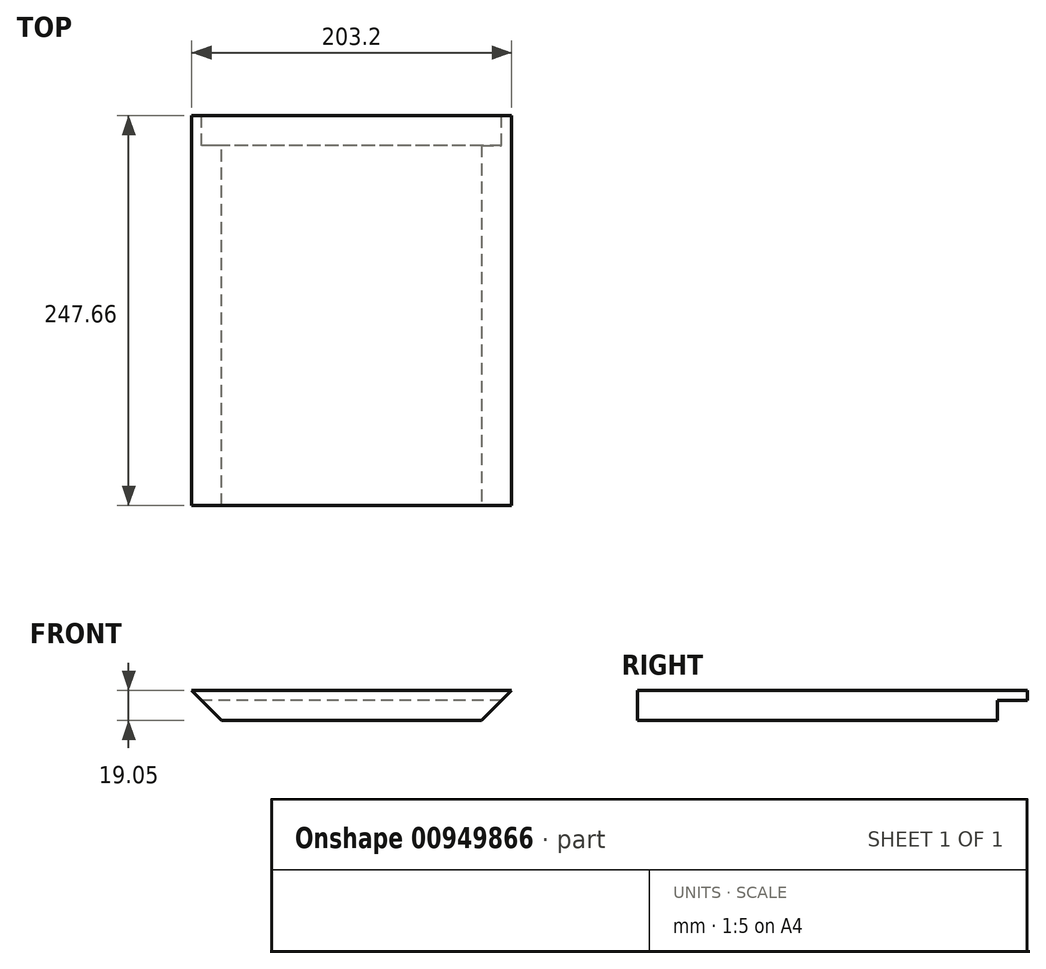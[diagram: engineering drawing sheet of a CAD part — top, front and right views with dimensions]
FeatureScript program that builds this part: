
annotation { "Feature Type Name" : "Feature", "Feature Type Description" : "" }
export const myFeature = defineFeature(function(context is Context, id is Id, definition is map)
    precondition{}
    {
        {
            var Q0;
            Q0=qCreatedBy(makeId("Top.planeOp"),FACE);
            var sketch = newSketch(context, id + "F0", { "sketchPlane" : qUnion([Q0])});
            skLineSegment(sketch, "E0.bottom", {"start": v(101.6, -123.83) * mm, "end": v(-101.6, -123.83) * mm});
            skLineSegment(sketch, "E0.top", {"start": v(101.6, 123.83) * mm, "end": v(-101.6, 123.83) * mm});
            skLineSegment(sketch, "E0.left", {"start": v(101.6, -123.83) * mm, "end": v(101.6, 123.83) * mm});
            skLineSegment(sketch, "E0.right", {"start": v(-101.6, -123.83) * mm, "end": v(-101.6, 123.83) * mm});
            skPoint(sketch, "E0.middle", {"position": v(0, 0) * mm});
            skSolve(sketch);
        }
        {
            var Q0;
            Q0 = qSketchRegion(id + "F0", true);
            extrude(context, id + "F1", {"entities" : qUnion([Q0]), "depth" : 19.05 * mm, "offsetDistance" : 25.4 * mm});
        }
        {
            var Q0;
            Q0=makeQuery(id+"F1.opExtrude","SWEPT_FACE",FACE,{"disambiguationData":[OSD([sQuery(id+"F0.wireOp",EDGE,"E0.right")])]});
            var sketch = newSketch(context, id + "F2", { "sketchPlane" : qUnion([Q0])});
            skLineSegment(sketch, "E1", {"start": v(-123.83, 12.7) * mm, "end": v(-104.78, 12.7) * mm});
            skLineSegment(sketch, "E2", {"start": v(-104.78, 12.7) * mm, "end": v(-104.78, 0) * mm});
            skLineSegment(sketch, "E3", {"start": v(-104.78, 0) * mm, "end": v(-123.83, 0) * mm});
            skLineSegment(sketch, "E4", {"start": v(-123.83, 0) * mm, "end": v(-123.83, 12.7) * mm});
            skSolve(sketch);
        }
        {
            var Q0;
            Q0 = qSketchRegion(id + "F2", true);
            extrude(context, id + "F3", {"entities" : qUnion([Q0]), "operationType" : NewBodyOperationType.REMOVE, "endBound" : BoundingType.THROUGH_ALL, "oppositeDirection" : true, "depth" : 25.4 * mm, "offsetDistance" : 25.4 * mm});
        }
        {
            var Q0;
            Q0=makeQuery(id+"F1.opExtrude","CAP_EDGE",EDGE,{"disambiguationData":[OSD([sQuery(id+"F0.wireOp",EDGE,"E0.right")])],"isStart":true});
            chamfer(context, id + "F4", {"entities" : qUnion([Q0]), "width" : 19.05 * mm, "tangentPropagation" : true});
        }
        {
            var Q0;
            Q0=makeQuery(id+"F1.opExtrude","CAP_EDGE",EDGE,{"disambiguationData":[OSD([sQuery(id+"F0.wireOp",EDGE,"E0.left")])],"isStart":true});
            chamfer(context, id + "F5", {"entities" : qUnion([Q0]), "width" : 19.05 * mm, "tangentPropagation" : true});
        }
    });
